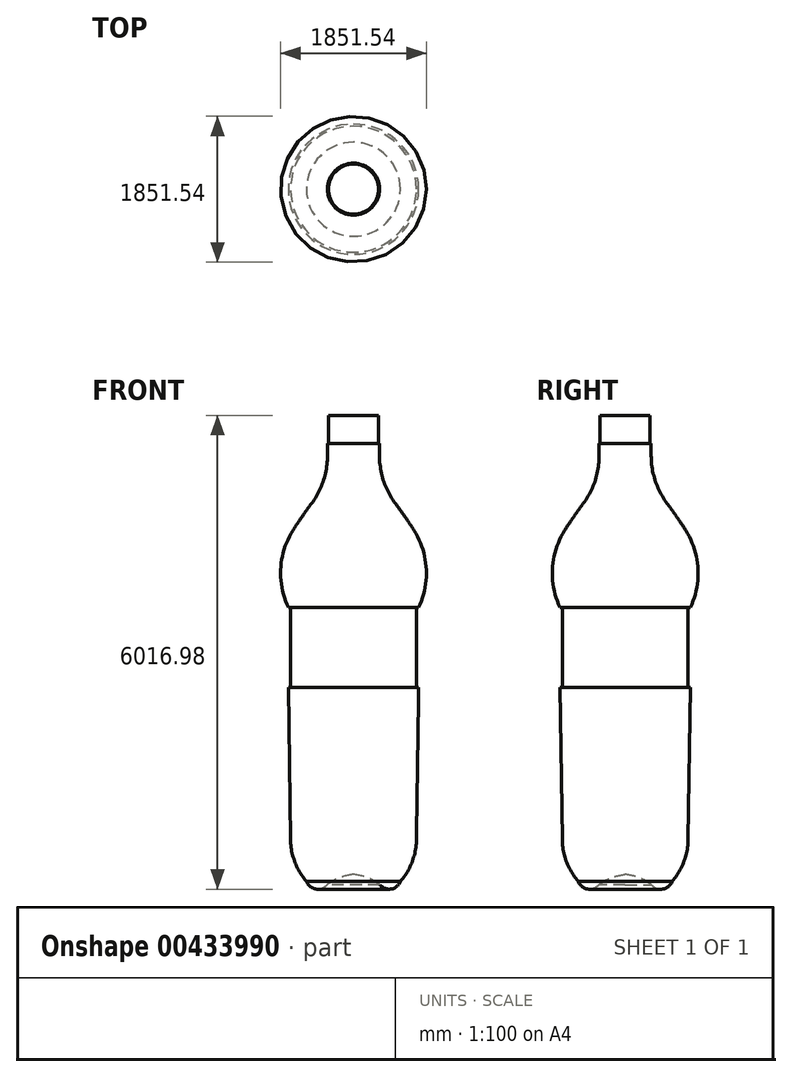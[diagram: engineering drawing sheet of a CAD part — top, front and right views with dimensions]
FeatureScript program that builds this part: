
annotation { "Feature Type Name" : "Feature", "Feature Type Description" : "" }
export const myFeature = defineFeature(function(context is Context, id is Id, definition is map)
    precondition{}
    {
        {
            var Q0;
            Q0=qCreatedBy(makeId("Front.planeOp"),FACE);
            var sketch = newSketch(context, id + "F0", { "sketchPlane" : qUnion([Q0])});
            skLineSegment(sketch, "E0", {"start": v(424.04, 2618.97) * mm, "end": v(424.04, -2778.53) * mm});
            skLineSegment(sketch, "E1", {"start": v(424.04, 2618.97) * mm, "end": v(106.54, 2618.97) * mm});
            skLineSegment(sketch, "E2", {"start": v(106.54, 2618.97) * mm, "end": v(106.54, 2263.37) * mm});
            skLineSegment(sketch, "E3", {"start": v(106.54, 2263.37) * mm, "end": v(93.84, 2263.37) * mm});
            skLineSegment(sketch, "E4", {"start": v(93.84, 2263.37) * mm, "end": v(93.84, 2110.97) * mm});
            skArc(sketch, "E5", {"start": v(-109.6, 1501.05) * mm, "mid": v(41.64, 1789.5) * mm, "end": v(93.84, 2110.97) * mm});
            skArc(sketch, "E6", {"start": v(-109.6, 1501.05) * mm, "mid": v(-231.04, 1332.18) * mm, "end": v(-345.46, 1158.47) * mm});
            skArc(sketch, "E7", {"start": v(-345.46, 1158.47) * mm, "mid": v(-499.93, 677.62) * mm, "end": v(-403.77, 181.8) * mm});
            skLineSegment(sketch, "E8", {"start": v(-403.77, 181.8) * mm, "end": v(-375.83, 181.8) * mm});
            skLineSegment(sketch, "E9", {"start": v(-375.83, 181.8) * mm, "end": v(-375.83, -834.2) * mm});
            skLineSegment(sketch, "E10", {"start": v(-375.83, -834.2) * mm, "end": v(-403.77, -834.2) * mm});
            skLineSegment(sketch, "E11", {"start": v(-403.77, -834.2) * mm, "end": v(-375.83, -2766.43) * mm});
            skLineSegment(sketch, "E12", {"start": v(424.04, -2778.53) * mm, "end": v(424.04, -3210.93) * mm});
            skPoint(sketch, "E13.endSnap0", {"position": v(36.69, -3401.43) * mm});
            skArc(sketch, "E14", {"start": v(-375.83, -2766.43) * mm, "mid": v(-321.2, -3050.5) * mm, "end": v(-172.17, -3298.45) * mm});
            skArc(sketch, "E15", {"start": v(424.04, -3210.93) * mm, "mid": v(246.45, -3252.57) * mm, "end": v(88.02, -3342.98) * mm});
            skArc(sketch, "E16", {"start": v(-172.17, -3298.45) * mm, "mid": v(-54.93, -3395.82) * mm, "end": v(88.02, -3342.98) * mm});
            skPoint(sketch, "E17.end.orphan", {"position": v(487.02, -3210.93) * mm});
            skPoint(sketch, "E17.start.orphan", {"position": v(487.02, -3401.43) * mm});
            skPoint(sketch, "E18.orphan", {"position": v(424.04, -3401.43) * mm});
            skPoint(sketch, "E19.end.orphan", {"position": v(-350.66, -3401.43) * mm});
            skSolve(sketch);
        }
        {
            var Q0;
            Q0 = qSketchRegion(id + "F0", true);
            var Q1;
            Q1=makeQuery(id+"F0.imprint","IMPRINT",FACE,{"disambiguationData":[TD([[makeQuery(id+"F0.imprint","IMPRINT",EDGE,{"derivedFrom":sQuery(id+"F0.wireOp",EDGE,"E0")}),-1.0]])]});
            var Q2;
            Q2=sQuery(id+"F0.wireOp",EDGE,"E0");
            revolve(context, id + "F1", {"entities" : qUnion([Q0, Q1]), "axis" : qUnion([Q2]), "revolveType" : RevolveType.FULL});
        }
    });
